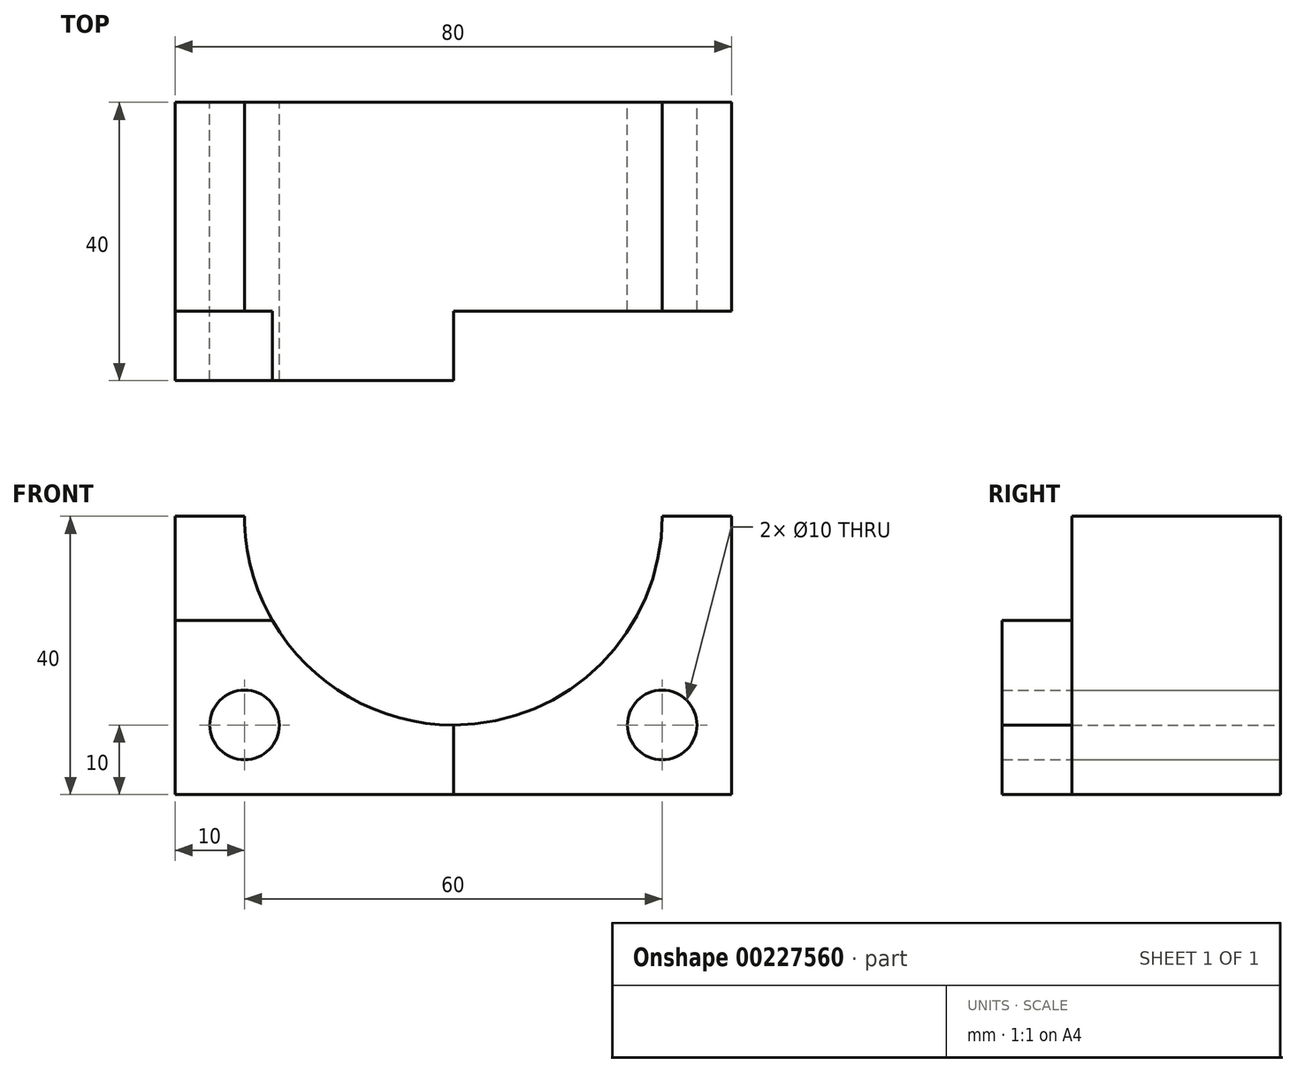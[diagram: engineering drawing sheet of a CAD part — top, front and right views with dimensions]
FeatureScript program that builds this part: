
annotation { "Feature Type Name" : "Feature", "Feature Type Description" : "" }
export const myFeature = defineFeature(function(context is Context, id is Id, definition is map)
    precondition{}
    {
        {
            var Q0;
            Q0=qCreatedBy(makeId("Front.planeOp"),FACE);
            var sketch = newSketch(context, id + "F0", { "sketchPlane" : qUnion([Q0])});
            skLineSegment(sketch, "E0", {"start": v(0, 0) * mm, "end": v(0, 40) * mm});
            skLineSegment(sketch, "E1", {"start": v(0, 0) * mm, "end": v(80, 0) * mm});
            skLineSegment(sketch, "E2", {"start": v(80, 0) * mm, "end": v(80, 40) * mm});
            skArc(sketch, "E3", {"start": v(10, 40) * mm, "mid": v(40, 10) * mm, "end": v(70, 40) * mm});
            skLineSegment(sketch, "E4", {"start": v(0, 40) * mm, "end": v(10, 40) * mm});
            skLineSegment(sketch, "E5", {"start": v(80, 40) * mm, "end": v(70, 40) * mm});
            skCircle(sketch, "E6", {"center": v(10, 10) * mm, "radius": 5 * mm});
            skCircle(sketch, "E7.MirrorC", {"center": v(70, 10) * mm, "radius": 5 * mm});
            skLineSegment(sketch, "E8", {"start": v(40, 10) * mm, "end": v(40, 0) * mm});
            skLineSegment(sketch, "E9", {"start": v(0, 25) * mm, "end": v(14.02, 25) * mm});
            skSolve(sketch);
        }
        {
            var Q0;
            {var subQ3=sQuery(id+"F0.wireOp",EDGE,"E2");Q0=makeQuery(id+"F0.imprint","IMPRINT",FACE,{"disambiguationData":[TD([[makeQuery(id+"F0.imprint","IMPRINT",EDGE,{"derivedFrom":subQ3}),1.0]])]});}
            var Q1;
            {var subQ0=sQuery(id+"F0.wireOp",EDGE,"E4");Q1=makeQuery(id+"F0.imprint","IMPRINT",FACE,{"disambiguationData":[TD([[makeQuery(id+"F0.imprint","IMPRINT",EDGE,{"derivedFrom":subQ0}),-1.0]])]});}
            extrude(context, id + "F1", {"entities" : qUnion([Q0, Q1]), "depth" : 30 * mm});
        }
        {
            var Q0;
            Q0=makeQuery(id+"F0.imprint","IMPRINT",FACE,{"disambiguationData":[TD([[makeQuery(id+"F0.imprint","IMPRINT",EDGE,{"derivedFrom":sQuery(id+"F0.wireOp",EDGE,"E6")}),-1.0]])]});
            extrude(context, id + "F2", {"entities" : qUnion([Q0]), "operationType" : NewBodyOperationType.ADD, "depth" : 40 * mm});
        }
    });
